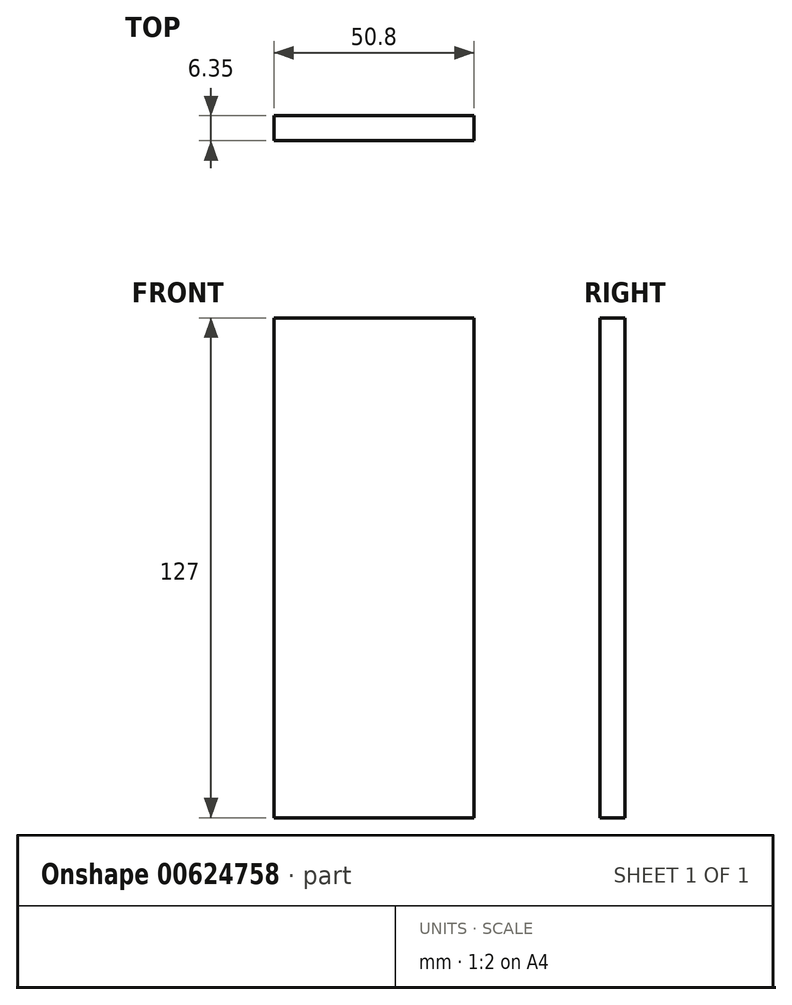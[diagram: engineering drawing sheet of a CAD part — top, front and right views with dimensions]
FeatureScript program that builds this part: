
annotation { "Feature Type Name" : "Feature", "Feature Type Description" : "" }
export const myFeature = defineFeature(function(context is Context, id is Id, definition is map)
    precondition{}
    {
        {
            var Q0;
            Q0=qCreatedBy(makeId("Front.planeOp"),FACE);
            var sketch = newSketch(context, id + "F0", { "sketchPlane" : qUnion([Q0])});
            skLineSegment(sketch, "E0.bottom", {"start": v(-25.4, 63.5) * mm, "end": v(25.4, 63.5) * mm});
            skLineSegment(sketch, "E0.top", {"start": v(-25.4, -63.5) * mm, "end": v(25.4, -63.5) * mm});
            skLineSegment(sketch, "E0.left", {"start": v(-25.4, 63.5) * mm, "end": v(-25.4, -63.5) * mm});
            skLineSegment(sketch, "E0.right", {"start": v(25.4, 63.5) * mm, "end": v(25.4, -63.5) * mm});
            skLineSegment(sketch, "E1", {"start": v(25.4, 63.5) * mm, "end": v(-25.4, -63.5) * mm});
            skSolve(sketch);
        }
        {
            var Q0;
            Q0 = qSketchRegion(id + "F0", true);
            extrude(context, id + "F1", {"entities" : qUnion([Q0]), "depth" : 6.35 * mm, "offsetDistance" : 25.4 * mm});
        }
    });
